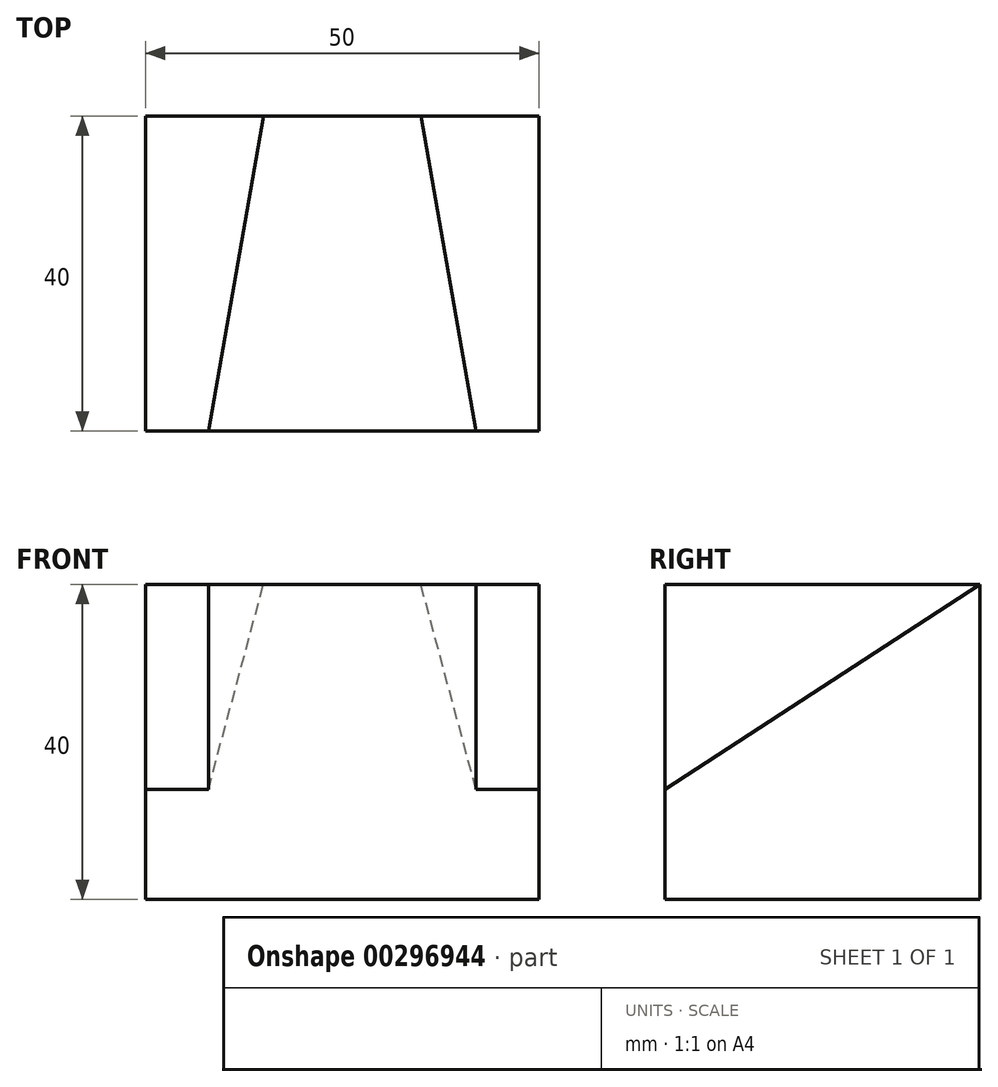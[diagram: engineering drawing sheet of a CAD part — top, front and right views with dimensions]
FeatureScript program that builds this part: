
annotation { "Feature Type Name" : "Feature", "Feature Type Description" : "" }
export const myFeature = defineFeature(function(context is Context, id is Id, definition is map)
    precondition{}
    {
        {
            var Q0;
            Q0=qCreatedBy(makeId("Right.planeOp"),FACE);
            var sketch = newSketch(context, id + "F0", { "sketchPlane" : qUnion([Q0])});
            skLineSegment(sketch, "E0.bottom", {"start": v(0, 0) * mm, "end": v(40, 0) * mm});
            skLineSegment(sketch, "E0.top", {"start": v(0, 40) * mm, "end": v(40, 40) * mm});
            skLineSegment(sketch, "E0.left", {"start": v(0, 0) * mm, "end": v(0, 40) * mm});
            skLineSegment(sketch, "E0.right", {"start": v(40, 0) * mm, "end": v(40, 40) * mm});
            skLineSegment(sketch, "E1", {"start": v(40, 40) * mm, "end": v(0, 14) * mm});
            skSolve(sketch);
        }
        {
            var Q0;
            {var subQ0=sQuery(id+"F0.wireOp",EDGE,"E0.bottom");Q0=makeQuery(id+"F0.imprint","IMPRINT",FACE,{"disambiguationData":[TD([[makeQuery(id+"F0.imprint","IMPRINT",EDGE,{"derivedFrom":subQ0}),1.0]])]});}
            extrude(context, id + "F1", {"entities" : qUnion([Q0]), "depth" : 50 * mm});
        }
        {
            var Q0;
            Q0=makeQuery(id+"F1.opExtrude","SWEPT_FACE",FACE,{"disambiguationData":[OSD([sQuery(id+"F0.wireOp",EDGE,"E0.bottom")])]});
            var sketch = newSketch(context, id + "F2", { "sketchPlane" : qUnion([Q0])});
            skLineSegment(sketch, "E2.bottom", {"start": v(8, 0) * mm, "end": v(42, 0) * mm});
            skLineSegment(sketch, "E2.top", {"start": v(8, -40) * mm, "end": v(42, -40) * mm});
            skLineSegment(sketch, "E2.left", {"start": v(8, 0) * mm, "end": v(8, -40) * mm});
            skLineSegment(sketch, "E2.right", {"start": v(42, 0) * mm, "end": v(42, -40) * mm});
            skLineSegment(sketch, "E3", {"start": v(42, 0) * mm, "end": v(35, -40) * mm});
            skLineSegment(sketch, "E4", {"start": v(8, 0) * mm, "end": v(15, -40) * mm});
            skSolve(sketch);
        }
        {
            var Q0;
            Q0=makeQuery(id+"F2.imprint","IMPRINT",FACE,{"disambiguationData":[TD([[makeQuery(id+"F2.imprint","IMPRINT",EDGE,{"derivedFrom":sQuery(id+"F2.wireOp",EDGE,"E2.bottom")}),1.0]])]});
            extrude(context, id + "F3", {"entities" : qUnion([Q0]), "operationType" : NewBodyOperationType.ADD, "oppositeDirection" : true, "depth" : 40 * mm});
        }
    });
